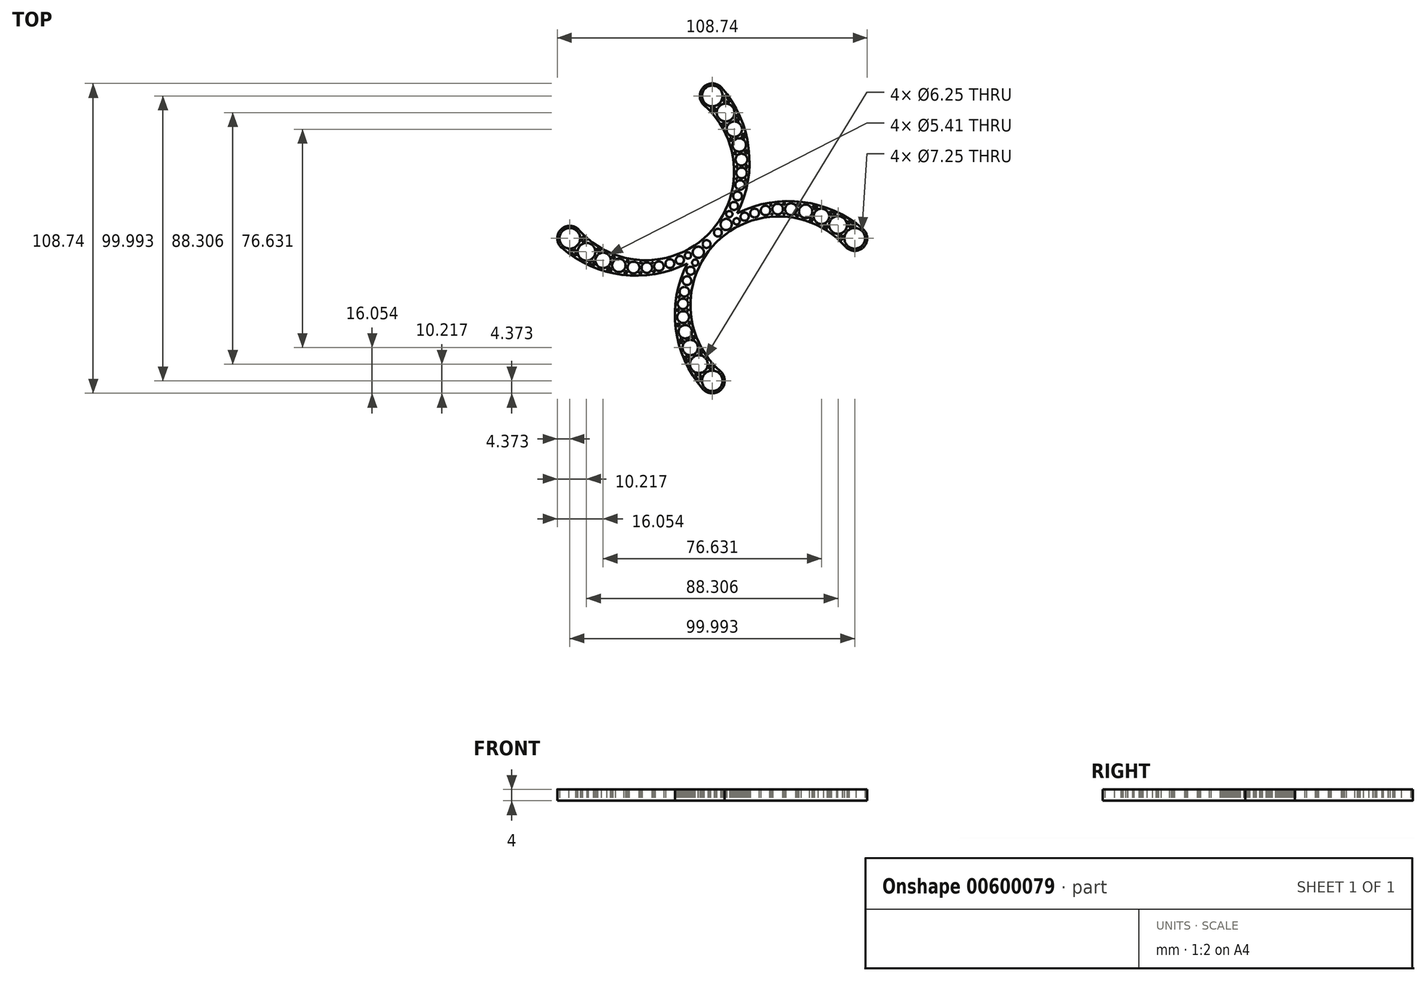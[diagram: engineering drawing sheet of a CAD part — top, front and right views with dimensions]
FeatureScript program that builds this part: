
annotation { "Feature Type Name" : "Feature", "Feature Type Description" : "" }
export const myFeature = defineFeature(function(context is Context, id is Id, definition is map)
    precondition{}
    {
        {
            var Q0;
            Q0=qCreatedBy(makeId("Top.planeOp"),FACE);
            var sketch = newSketch(context, id + "F0", { "sketchPlane" : qUnion([Q0])});
            skCircle(sketch, "E0.1.0", {"center": v(-50, 0) * mm, "radius": 3.62 * mm});
            skArc(sketch, "E0.1.1", {"start": v(-50.38, -4.36) * mm, "mid": v(-49.12, -4.29) * mm, "end": v(-47.93, -3.86) * mm});
            skArc(sketch, "E1", {"start": v(-46.7, 2.89) * mm, "mid": v(-24.38, -7.66) * mm, "end": v(-1.41, 1.41) * mm});
            skArc(sketch, "E2", {"start": v(-52.87, -3.3) * mm, "mid": v(-31.68, -12.77) * mm, "end": v(-8.81, -8.81) * mm});
            skArc(sketch, "E3.0", {"start": v(-50.38, -4.36) * mm, "mid": v(-49.07, -5.31) * mm, "end": v(-47.72, -6.21) * mm});
            skArc(sketch, "E4.0", {"start": v(-45.68, 0.7) * mm, "mid": v(-44.86, -0.08) * mm, "end": v(-44, -0.83) * mm});
            skPoint(sketch, "E5.orphan", {"position": v(-52.38, -2.74) * mm});
            skPoint(sketch, "E6.orphan", {"position": v(-47.27, 2.4) * mm});
            skArc(sketch, "E7.trimOffspring", {"start": v(-46.7, 2.89) * mm, "mid": v(-53.1, 3.09) * mm, "end": v(-52.87, -3.3) * mm});
            skArc(sketch, "E8", {"start": v(-47.93, -3.86) * mm, "mid": v(-48.01, -5.05) * mm, "end": v(-47.72, -6.21) * mm});
            skArc(sketch, "E9", {"start": v(-41.77, -7.75) * mm, "mid": v(-41.64, -8.67) * mm, "end": v(-41.27, -9.52) * mm});
            skCircle(sketch, "E10.0", {"center": v(-44.15, -4.7) * mm, "radius": 3.12 * mm});
            skCircle(sketch, "E11.0", {"center": v(-38.32, -7.73) * mm, "radius": 2.7 * mm});
            skArc(sketch, "E12", {"start": v(-33.98, -6.6) * mm, "mid": v(-34.47, -6.87) * mm, "end": v(-34.9, -7.2) * mm});
            skArc(sketch, "E13", {"start": v(-29.22, -7.89) * mm, "mid": v(-29.55, -8.15) * mm, "end": v(-29.84, -8.45) * mm});
            skArc(sketch, "E14", {"start": v(-24.77, -8.4) * mm, "mid": v(-24.98, -8.63) * mm, "end": v(-25.16, -8.89) * mm});
            skCircle(sketch, "E15.0", {"center": v(-32.77, -9.47) * mm, "radius": 2.36 * mm});
            skCircle(sketch, "E16.0", {"center": v(-27.65, -10.24) * mm, "radius": 2.08 * mm});
            skCircle(sketch, "E17.0", {"center": v(-22.97, -10.28) * mm, "radius": 1.85 * mm});
            skArc(sketch, "E18", {"start": v(-20.65, -8.31) * mm, "mid": v(-20.78, -8.5) * mm, "end": v(-20.9, -8.7) * mm});
            skCircle(sketch, "E19.0", {"center": v(-18.72, -9.78) * mm, "radius": 1.67 * mm});
            skCircle(sketch, "E20.0", {"center": v(-14.87, -8.86) * mm, "radius": 1.54 * mm});
            skCircle(sketch, "E21.0", {"center": v(-11.37, -7.62) * mm, "radius": 1.43 * mm});
            skCircle(sketch, "E22.0", {"center": v(-8.52, -5.99) * mm, "radius": 1.1 * mm});
            skCircle(sketch, "E23.0", {"center": v(-4.88, -4.88) * mm, "radius": 1.96 * mm});
            skCircle(sketch, "E24.0", {"center": v(-2, -2) * mm, "radius": 1.37 * mm});
            skArc(sketch, "E25.trimOffspring", {"start": v(-45.79, -1.19) * mm, "mid": v(-45.63, -0.25) * mm, "end": v(-45.68, 0.7) * mm});
            skArc(sketch, "E26.trimOffspring", {"start": v(-44, -0.83) * mm, "mid": v(-44.92, -0.9) * mm, "end": v(-45.79, -1.19) * mm});
            skArc(sketch, "E27.trimOffspring", {"start": v(-40.5, -3.43) * mm, "mid": v(-39.74, -3.9) * mm, "end": v(-38.97, -4.34) * mm});
            skArc(sketch, "E28.trimOffspring", {"start": v(-43.54, -8.53) * mm, "mid": v(-42.41, -9.04) * mm, "end": v(-41.27, -9.52) * mm});
            skArc(sketch, "E29.trimOffspring", {"start": v(-43.54, -8.53) * mm, "mid": v(-42.6, -8.25) * mm, "end": v(-41.77, -7.75) * mm});
            skArc(sketch, "E30.trimOffspring", {"start": v(-35.26, -6.13) * mm, "mid": v(-34.62, -6.37) * mm, "end": v(-33.98, -6.6) * mm});
            skArc(sketch, "E31.trimOffspring", {"start": v(-38.97, -4.34) * mm, "mid": v(-39.66, -4.55) * mm, "end": v(-40.28, -4.9) * mm});
            skArc(sketch, "E32.trimOffspring", {"start": v(-40.28, -4.9) * mm, "mid": v(-40.32, -4.15) * mm, "end": v(-40.5, -3.43) * mm});
            skArc(sketch, "E33.trimOffspring", {"start": v(-37.05, -10.94) * mm, "mid": v(-36.38, -10.6) * mm, "end": v(-35.81, -10.1) * mm});
            skArc(sketch, "E34.trimOffspring", {"start": v(-37.05, -10.94) * mm, "mid": v(-36.13, -11.18) * mm, "end": v(-35.2, -11.4) * mm});
            skArc(sketch, "E35.trimOffspring", {"start": v(-30.23, -7.68) * mm, "mid": v(-29.73, -7.79) * mm, "end": v(-29.22, -7.89) * mm});
            skArc(sketch, "E36.trimOffspring", {"start": v(-34.9, -7.2) * mm, "mid": v(-35.04, -6.65) * mm, "end": v(-35.26, -6.13) * mm});
            skArc(sketch, "E37.trimOffspring", {"start": v(-35.81, -10.1) * mm, "mid": v(-35.59, -10.79) * mm, "end": v(-35.2, -11.4) * mm});
            skArc(sketch, "E38.trimOffspring", {"start": v(-31.1, -12.08) * mm, "mid": v(-30.38, -12.16) * mm, "end": v(-29.66, -12.22) * mm});
            skArc(sketch, "E39.trimOffspring", {"start": v(-31.1, -12.08) * mm, "mid": v(-30.64, -11.73) * mm, "end": v(-30.26, -11.3) * mm});
            skArc(sketch, "E40.trimOffspring", {"start": v(-30.26, -11.3) * mm, "mid": v(-30, -11.79) * mm, "end": v(-29.66, -12.22) * mm});
            skArc(sketch, "E41.trimOffspring", {"start": v(-29.84, -8.45) * mm, "mid": v(-30, -8.05) * mm, "end": v(-30.23, -7.68) * mm});
            skArc(sketch, "E42.trimOffspring", {"start": v(-25.19, -11.64) * mm, "mid": v(-24.94, -11.97) * mm, "end": v(-24.65, -12.27) * mm});
            skArc(sketch, "E43.trimOffspring", {"start": v(-25.16, -8.89) * mm, "mid": v(-25.33, -8.61) * mm, "end": v(-25.53, -8.36) * mm});
            skArc(sketch, "E44.trimOffspring", {"start": v(-20.58, -11.33) * mm, "mid": v(-20.37, -11.56) * mm, "end": v(-20.12, -11.76) * mm});
            skArc(sketch, "E45.trimOffspring", {"start": v(-20.9, -8.7) * mm, "mid": v(-21.04, -8.53) * mm, "end": v(-21.21, -8.36) * mm});
            skArc(sketch, "E46.trimOffspring", {"start": v(-21.21, -8.36) * mm, "mid": v(-20.93, -8.34) * mm, "end": v(-20.65, -8.31) * mm});
            skArc(sketch, "E47.trimOffspring", {"start": v(-25.73, -12.31) * mm, "mid": v(-25.19, -12.3) * mm, "end": v(-24.65, -12.27) * mm});
            skArc(sketch, "E48.trimOffspring", {"start": v(-25.73, -12.31) * mm, "mid": v(-25.43, -12) * mm, "end": v(-25.19, -11.64) * mm});
            skArc(sketch, "E49.trimOffspring", {"start": v(-20.92, -11.89) * mm, "mid": v(-20.73, -11.62) * mm, "end": v(-20.58, -11.33) * mm});
            skArc(sketch, "E50.trimOffspring", {"start": v(-20.92, -11.89) * mm, "mid": v(-20.52, -11.83) * mm, "end": v(-20.12, -11.76) * mm});
            skLineSegment(sketch, "E51", {"start": v(-25.53, -8.36) * mm, "end": v(-24.77, -8.4) * mm});
            skArc(sketch, "E52.2.MirrorCS", {"start": v(-6.6, -33.98) * mm, "mid": v(-6.87, -34.47) * mm, "end": v(-7.2, -34.9) * mm});
            skArc(sketch, "E52.3.MirrorCS", {"start": v(-7.2, -34.9) * mm, "mid": v(-6.65, -35.04) * mm, "end": v(-6.13, -35.26) * mm});
            skCircle(sketch, "E52.4.MirrorC", {"center": v(-5.99, -8.52) * mm, "radius": 1.1 * mm});
            skArc(sketch, "E52.8.MirrorCS", {"start": v(-6.13, -35.26) * mm, "mid": v(-6.37, -34.62) * mm, "end": v(-6.6, -33.98) * mm});
            skArc(sketch, "E52.9.MirrorCS", {"start": v(-11.89, -20.92) * mm, "mid": v(-11.62, -20.73) * mm, "end": v(-11.33, -20.58) * mm});
            skArc(sketch, "E52.10.MirrorCS", {"start": v(-8.89, -25.16) * mm, "mid": v(-8.61, -25.33) * mm, "end": v(-8.36, -25.53) * mm});
            skArc(sketch, "E52.11.MirrorCS", {"start": v(-8.4, -24.77) * mm, "mid": v(-8.63, -24.98) * mm, "end": v(-8.89, -25.16) * mm});
            skLineSegment(sketch, "E52.13.MirrorCS", {"start": v(-8.36, -25.53) * mm, "end": v(-8.4, -24.77) * mm});
            skArc(sketch, "E52.14.MirrorCS", {"start": v(-8.31, -20.65) * mm, "mid": v(-8.5, -20.78) * mm, "end": v(-8.7, -20.9) * mm});
            skArc(sketch, "E52.18.MirrorCS", {"start": v(-10.1, -35.81) * mm, "mid": v(-10.79, -35.59) * mm, "end": v(-11.4, -35.2) * mm});
            skArc(sketch, "E52.19.MirrorCS", {"start": v(-10.94, -37.05) * mm, "mid": v(-10.6, -36.38) * mm, "end": v(-10.1, -35.81) * mm});
            skCircle(sketch, "E52.20.MirrorC", {"center": v(-7.62, -11.37) * mm, "radius": 1.43 * mm});
            skArc(sketch, "E52.21.MirrorCS", {"start": v(-10.94, -37.05) * mm, "mid": v(-11.18, -36.13) * mm, "end": v(-11.4, -35.2) * mm});
            skArc(sketch, "E52.22.MirrorCS", {"start": v(-4.36, -50.38) * mm, "mid": v(-5.31, -49.07) * mm, "end": v(-6.21, -47.72) * mm});
            skArc(sketch, "E52.23.MirrorCS", {"start": v(0.7, -45.68) * mm, "mid": v(-0.08, -44.86) * mm, "end": v(-0.83, -44) * mm});
            skArc(sketch, "E52.24.MirrorCS", {"start": v(-4.36, -50.38) * mm, "mid": v(-4.29, -49.12) * mm, "end": v(-3.86, -47.93) * mm});
            skArc(sketch, "E52.25.MirrorCS", {"start": v(-11.89, -20.92) * mm, "mid": v(-11.83, -20.52) * mm, "end": v(-11.76, -20.12) * mm});
            skArc(sketch, "E52.27.MirrorCS", {"start": v(-12.31, -25.73) * mm, "mid": v(-12, -25.43) * mm, "end": v(-11.64, -25.19) * mm});
            skArc(sketch, "E52.28.MirrorCS", {"start": v(-12.08, -31.1) * mm, "mid": v(-11.73, -30.64) * mm, "end": v(-11.3, -30.26) * mm});
            skCircle(sketch, "E52.29.MirrorC", {"center": v(-8.86, -14.87) * mm, "radius": 1.54 * mm});
            skArc(sketch, "E52.30.MirrorCS", {"start": v(-12.08, -31.1) * mm, "mid": v(-12.16, -30.38) * mm, "end": v(-12.22, -29.66) * mm});
            skArc(sketch, "E52.31.MirrorCS", {"start": v(-7.68, -30.23) * mm, "mid": v(-7.79, -29.73) * mm, "end": v(-7.89, -29.22) * mm});
            skArc(sketch, "E52.32.MirrorCS", {"start": v(-11.33, -20.58) * mm, "mid": v(-11.56, -20.37) * mm, "end": v(-11.76, -20.12) * mm});
            skArc(sketch, "E52.34.MirrorCS", {"start": v(-12.31, -25.73) * mm, "mid": v(-12.3, -25.19) * mm, "end": v(-12.27, -24.65) * mm});
            skArc(sketch, "E52.35.MirrorCS", {"start": v(-8.36, -21.21) * mm, "mid": v(-8.34, -20.93) * mm, "end": v(-8.31, -20.65) * mm});
            skArc(sketch, "E52.37.MirrorCS", {"start": v(-11.3, -30.26) * mm, "mid": v(-11.79, -30) * mm, "end": v(-12.22, -29.66) * mm});
            skArc(sketch, "E52.38.MirrorCS", {"start": v(-3.86, -47.93) * mm, "mid": v(-5.05, -48.01) * mm, "end": v(-6.21, -47.72) * mm});
            skArc(sketch, "E52.41.MirrorCS", {"start": v(-1.19, -45.79) * mm, "mid": v(-0.25, -45.63) * mm, "end": v(0.7, -45.68) * mm});
            skArc(sketch, "E52.42.MirrorCS", {"start": v(-8.45, -29.84) * mm, "mid": v(-8.05, -30) * mm, "end": v(-7.68, -30.23) * mm});
            skArc(sketch, "E52.43.MirrorCS", {"start": v(-7.89, -29.22) * mm, "mid": v(-8.15, -29.55) * mm, "end": v(-8.45, -29.84) * mm});
            skArc(sketch, "E52.44.MirrorCS", {"start": v(-11.64, -25.19) * mm, "mid": v(-11.97, -24.94) * mm, "end": v(-12.27, -24.65) * mm});
            skArc(sketch, "E52.47.MirrorCS", {"start": v(-8.7, -20.9) * mm, "mid": v(-8.53, -21.04) * mm, "end": v(-8.36, -21.21) * mm});
            skArc(sketch, "E52.48.MirrorCS", {"start": v(-4.9, -40.28) * mm, "mid": v(-4.15, -40.32) * mm, "end": v(-3.43, -40.5) * mm});
            skArc(sketch, "E52.49.MirrorCS", {"start": v(-7.75, -41.77) * mm, "mid": v(-8.67, -41.64) * mm, "end": v(-9.52, -41.27) * mm});
            skArc(sketch, "E52.50.MirrorCS", {"start": v(-8.53, -43.54) * mm, "mid": v(-9.04, -42.41) * mm, "end": v(-9.52, -41.27) * mm});
            skArc(sketch, "E52.51.MirrorCS", {"start": v(-4.34, -38.97) * mm, "mid": v(-4.55, -39.66) * mm, "end": v(-4.9, -40.28) * mm});
            skArc(sketch, "E52.52.MirrorCS", {"start": v(-3.43, -40.5) * mm, "mid": v(-3.9, -39.74) * mm, "end": v(-4.34, -38.97) * mm});
            skArc(sketch, "E52.53.MirrorCS", {"start": v(-0.83, -44) * mm, "mid": v(-0.9, -44.92) * mm, "end": v(-1.19, -45.79) * mm});
            skArc(sketch, "E52.54.MirrorCS", {"start": v(-8.53, -43.54) * mm, "mid": v(-8.25, -42.6) * mm, "end": v(-7.75, -41.77) * mm});
            skPoint(sketch, "E52.55.MirrorP", {"position": v(2.4, -47.27) * mm});
            skArc(sketch, "E52.56.MirrorCS", {"start": v(-3.3, -52.87) * mm, "mid": v(-12.77, -31.68) * mm, "end": v(-8.81, -8.81) * mm});
            skCircle(sketch, "E52.57.MirrorC", {"center": v(0, -50) * mm, "radius": 3.62 * mm});
            skCircle(sketch, "E52.58.MirrorC", {"center": v(-7.73, -38.32) * mm, "radius": 2.7 * mm});
            skCircle(sketch, "E52.59.MirrorC", {"center": v(-10.28, -22.97) * mm, "radius": 1.85 * mm});
            skArc(sketch, "E52.60.MirrorCS", {"start": v(2.89, -46.7) * mm, "mid": v(3.09, -53.1) * mm, "end": v(-3.3, -52.87) * mm});
            skCircle(sketch, "E52.61.MirrorC", {"center": v(-9.78, -18.72) * mm, "radius": 1.67 * mm});
            skCircle(sketch, "E52.62.MirrorC", {"center": v(-4.7, -44.15) * mm, "radius": 3.12 * mm});
            skCircle(sketch, "E52.63.MirrorC", {"center": v(-9.47, -32.77) * mm, "radius": 2.36 * mm});
            skCircle(sketch, "E52.64.MirrorC", {"center": v(-10.24, -27.65) * mm, "radius": 2.08 * mm});
            skPoint(sketch, "E52.65.MirrorP", {"position": v(-2.74, -52.38) * mm});
            skArc(sketch, "E53.0.MirrorCS", {"start": v(2.89, -46.7) * mm, "mid": v(-7.66, -24.38) * mm, "end": v(1.41, -1.41) * mm});
            skLineSegment(sketch, "E54.11.MirrorCS", {"start": v(8.36, 25.53) * mm, "end": v(8.4, 24.77) * mm});
            skCircle(sketch, "E54.13.MirrorC", {"center": v(5.99, 8.52) * mm, "radius": 1.1 * mm});
            skCircle(sketch, "E54.15.MirrorC", {"center": v(7.62, 11.37) * mm, "radius": 1.43 * mm});
            skArc(sketch, "E54.20.MirrorCS", {"start": v(8.36, 21.21) * mm, "mid": v(8.34, 20.93) * mm, "end": v(8.31, 20.65) * mm});
            skArc(sketch, "E54.21.MirrorCS", {"start": v(20.65, 8.31) * mm, "mid": v(20.78, 8.5) * mm, "end": v(20.9, 8.7) * mm});
            skArc(sketch, "E54.22.MirrorCS", {"start": v(25.19, 11.64) * mm, "mid": v(24.94, 11.97) * mm, "end": v(24.65, 12.27) * mm});
            skArc(sketch, "E54.23.MirrorCS", {"start": v(8.4, 24.77) * mm, "mid": v(8.63, 24.98) * mm, "end": v(8.89, 25.16) * mm});
            skArc(sketch, "E54.25.MirrorCS", {"start": v(11.33, 20.58) * mm, "mid": v(11.56, 20.37) * mm, "end": v(11.76, 20.12) * mm});
            skArc(sketch, "E54.27.MirrorCS", {"start": v(12.31, 25.73) * mm, "mid": v(12, 25.43) * mm, "end": v(11.64, 25.19) * mm});
            skArc(sketch, "E54.31.MirrorCS", {"start": v(8.89, 25.16) * mm, "mid": v(8.61, 25.33) * mm, "end": v(8.36, 25.53) * mm});
            skArc(sketch, "E54.33.MirrorCS", {"start": v(8.7, 20.9) * mm, "mid": v(8.53, 21.04) * mm, "end": v(8.36, 21.21) * mm});
            skArc(sketch, "E54.34.MirrorCS", {"start": v(12.31, 25.73) * mm, "mid": v(12.3, 25.19) * mm, "end": v(12.27, 24.65) * mm});
            skArc(sketch, "E54.35.MirrorCS", {"start": v(20.9, 8.7) * mm, "mid": v(21.04, 8.53) * mm, "end": v(21.21, 8.36) * mm});
            skArc(sketch, "E54.36.MirrorCS", {"start": v(30.23, 7.68) * mm, "mid": v(29.73, 7.79) * mm, "end": v(29.22, 7.89) * mm});
            skArc(sketch, "E54.37.MirrorCS", {"start": v(7.68, 30.23) * mm, "mid": v(7.79, 29.73) * mm, "end": v(7.89, 29.22) * mm});
            skArc(sketch, "E54.38.MirrorCS", {"start": v(8.31, 20.65) * mm, "mid": v(8.5, 20.78) * mm, "end": v(8.7, 20.9) * mm});
            skArc(sketch, "E54.41.MirrorCS", {"start": v(11.64, 25.19) * mm, "mid": v(11.97, 24.94) * mm, "end": v(12.27, 24.65) * mm});
            skCircle(sketch, "E54.42.MirrorC", {"center": v(14.87, 8.86) * mm, "radius": 1.54 * mm});
            skCircle(sketch, "E54.44.MirrorC", {"center": v(8.52, 5.99) * mm, "radius": 1.1 * mm});
            skArc(sketch, "E54.47.MirrorCS", {"start": v(10.1, 35.81) * mm, "mid": v(10.79, 35.59) * mm, "end": v(11.4, 35.2) * mm});
            skArc(sketch, "E54.48.MirrorCS", {"start": v(4.36, 50.38) * mm, "mid": v(4.29, 49.12) * mm, "end": v(3.86, 47.93) * mm});
            skArc(sketch, "E54.49.MirrorCS", {"start": v(10.94, 37.05) * mm, "mid": v(11.18, 36.13) * mm, "end": v(11.4, 35.2) * mm});
            skArc(sketch, "E54.50.MirrorCS", {"start": v(29.84, 8.45) * mm, "mid": v(30, 8.05) * mm, "end": v(30.23, 7.68) * mm});
            skArc(sketch, "E54.51.MirrorCS", {"start": v(31.1, 12.08) * mm, "mid": v(30.38, 12.16) * mm, "end": v(29.66, 12.22) * mm});
            skCircle(sketch, "E54.53.MirrorC", {"center": v(18.72, 9.78) * mm, "radius": 1.67 * mm});
            skArc(sketch, "E54.54.MirrorCS", {"start": v(-0.7, 45.68) * mm, "mid": v(0.08, 44.86) * mm, "end": v(0.83, 44) * mm});
            skArc(sketch, "E54.55.MirrorCS", {"start": v(4.36, 50.38) * mm, "mid": v(5.31, 49.07) * mm, "end": v(6.21, 47.72) * mm});
            skArc(sketch, "E54.56.MirrorCS", {"start": v(3.86, 47.93) * mm, "mid": v(5.05, 48.01) * mm, "end": v(6.21, 47.72) * mm});
            skArc(sketch, "E54.57.MirrorCS", {"start": v(7.89, 29.22) * mm, "mid": v(8.15, 29.55) * mm, "end": v(8.45, 29.84) * mm});
            skArc(sketch, "E54.59.MirrorCS", {"start": v(6.13, 35.26) * mm, "mid": v(6.37, 34.62) * mm, "end": v(6.6, 33.98) * mm});
            skArc(sketch, "E54.62.MirrorCS", {"start": v(11.89, 20.92) * mm, "mid": v(11.62, 20.73) * mm, "end": v(11.33, 20.58) * mm});
            skArc(sketch, "E54.63.MirrorCS", {"start": v(35.26, 6.13) * mm, "mid": v(34.62, 6.37) * mm, "end": v(33.98, 6.6) * mm});
            skArc(sketch, "E54.64.MirrorCS", {"start": v(25.73, 12.31) * mm, "mid": v(25.43, 12) * mm, "end": v(25.19, 11.64) * mm});
            skArc(sketch, "E54.65.MirrorCS", {"start": v(10.94, 37.05) * mm, "mid": v(10.6, 36.38) * mm, "end": v(10.1, 35.81) * mm});
            skArc(sketch, "E54.66.MirrorCS", {"start": v(29.22, 7.89) * mm, "mid": v(29.55, 8.15) * mm, "end": v(29.84, 8.45) * mm});
            skArc(sketch, "E54.67.MirrorCS", {"start": v(6.6, 33.98) * mm, "mid": v(6.87, 34.47) * mm, "end": v(7.2, 34.9) * mm});
            skCircle(sketch, "E54.68.MirrorC", {"center": v(4.88, 4.88) * mm, "radius": 1.96 * mm});
            skArc(sketch, "E54.69.MirrorCS", {"start": v(7.2, 34.9) * mm, "mid": v(6.65, 35.04) * mm, "end": v(6.13, 35.26) * mm});
            skArc(sketch, "E54.70.MirrorCS", {"start": v(20.58, 11.33) * mm, "mid": v(20.37, 11.56) * mm, "end": v(20.12, 11.76) * mm});
            skArc(sketch, "E54.71.MirrorCS", {"start": v(34.9, 7.2) * mm, "mid": v(35.04, 6.65) * mm, "end": v(35.26, 6.13) * mm});
            skArc(sketch, "E54.72.MirrorCS", {"start": v(40.28, 4.9) * mm, "mid": v(40.32, 4.15) * mm, "end": v(40.5, 3.43) * mm});
            skArc(sketch, "E54.73.MirrorCS", {"start": v(4.9, 40.28) * mm, "mid": v(4.15, 40.32) * mm, "end": v(3.43, 40.5) * mm});
            skCircle(sketch, "E54.74.MirrorC", {"center": v(8.86, 14.87) * mm, "radius": 1.54 * mm});
            skArc(sketch, "E54.76.MirrorCS", {"start": v(38.97, 4.34) * mm, "mid": v(39.66, 4.55) * mm, "end": v(40.28, 4.9) * mm});
            skArc(sketch, "E54.77.MirrorCS", {"start": v(21.21, 8.36) * mm, "mid": v(20.93, 8.34) * mm, "end": v(20.65, 8.31) * mm});
            skArc(sketch, "E54.78.MirrorCS", {"start": v(1.19, 45.79) * mm, "mid": v(0.25, 45.63) * mm, "end": v(-0.7, 45.68) * mm});
            skArc(sketch, "E54.80.MirrorCS", {"start": v(25.73, 12.31) * mm, "mid": v(25.19, 12.3) * mm, "end": v(24.65, 12.27) * mm});
            skArc(sketch, "E54.81.MirrorCS", {"start": v(33.98, 6.6) * mm, "mid": v(34.47, 6.87) * mm, "end": v(34.9, 7.2) * mm});
            skArc(sketch, "E54.82.MirrorCS", {"start": v(45.68, -0.7) * mm, "mid": v(44.86, 0.08) * mm, "end": v(44, 0.83) * mm});
            skArc(sketch, "E54.83.MirrorCS", {"start": v(20.92, 11.89) * mm, "mid": v(20.73, 11.62) * mm, "end": v(20.58, 11.33) * mm});
            skArc(sketch, "E54.84.MirrorCS", {"start": v(20.92, 11.89) * mm, "mid": v(20.52, 11.83) * mm, "end": v(20.12, 11.76) * mm});
            skArc(sketch, "E54.85.MirrorCS", {"start": v(45.79, 1.19) * mm, "mid": v(45.63, 0.25) * mm, "end": v(45.68, -0.7) * mm});
            skArc(sketch, "E54.86.MirrorCS", {"start": v(12.08, 31.1) * mm, "mid": v(11.73, 30.64) * mm, "end": v(11.3, 30.26) * mm});
            skCircle(sketch, "E54.89.MirrorC", {"center": v(11.37, 7.62) * mm, "radius": 1.43 * mm});
            skArc(sketch, "E54.90.MirrorCS", {"start": v(4.34, 38.97) * mm, "mid": v(4.55, 39.66) * mm, "end": v(4.9, 40.28) * mm});
            skCircle(sketch, "E54.91.MirrorC", {"center": v(9.78, 18.72) * mm, "radius": 1.67 * mm});
            skArc(sketch, "E54.92.MirrorCS", {"start": v(25.16, 8.89) * mm, "mid": v(25.33, 8.61) * mm, "end": v(25.53, 8.36) * mm});
            skArc(sketch, "E54.93.MirrorCS", {"start": v(11.89, 20.92) * mm, "mid": v(11.83, 20.52) * mm, "end": v(11.76, 20.12) * mm});
            skArc(sketch, "E54.94.MirrorCS", {"start": v(8.45, 29.84) * mm, "mid": v(8.05, 30) * mm, "end": v(7.68, 30.23) * mm});
            skArc(sketch, "E54.95.MirrorCS", {"start": v(3.43, 40.5) * mm, "mid": v(3.9, 39.74) * mm, "end": v(4.34, 38.97) * mm});
            skCircle(sketch, "E54.96.MirrorC", {"center": v(7.73, 38.32) * mm, "radius": 2.7 * mm});
            skArc(sketch, "E54.97.MirrorCS", {"start": v(44, 0.83) * mm, "mid": v(44.92, 0.9) * mm, "end": v(45.79, 1.19) * mm});
            skArc(sketch, "E54.98.MirrorCS", {"start": v(37.05, 10.94) * mm, "mid": v(36.13, 11.18) * mm, "end": v(35.2, 11.4) * mm});
            skArc(sketch, "E54.99.MirrorCS", {"start": v(30.26, 11.3) * mm, "mid": v(30, 11.79) * mm, "end": v(29.66, 12.22) * mm});
            skArc(sketch, "E54.100.MirrorCS", {"start": v(12.08, 31.1) * mm, "mid": v(12.16, 30.38) * mm, "end": v(12.22, 29.66) * mm});
            skArc(sketch, "E54.101.MirrorCS", {"start": v(43.54, 8.53) * mm, "mid": v(42.6, 8.25) * mm, "end": v(41.77, 7.75) * mm});
            skCircle(sketch, "E54.102.MirrorC", {"center": v(4.7, 44.15) * mm, "radius": 3.12 * mm});
            skCircle(sketch, "E54.103.MirrorC", {"center": v(9.47, 32.77) * mm, "radius": 2.36 * mm});
            skArc(sketch, "E54.104.MirrorCS", {"start": v(40.5, 3.43) * mm, "mid": v(39.74, 3.9) * mm, "end": v(38.97, 4.34) * mm});
            skArc(sketch, "E54.105.MirrorCS", {"start": v(41.77, 7.75) * mm, "mid": v(41.64, 8.67) * mm, "end": v(41.27, 9.52) * mm});
            skArc(sketch, "E54.106.MirrorCS", {"start": v(50.38, 4.36) * mm, "mid": v(49.12, 4.29) * mm, "end": v(47.93, 3.86) * mm});
            skArc(sketch, "E54.107.MirrorCS", {"start": v(7.75, 41.77) * mm, "mid": v(8.67, 41.64) * mm, "end": v(9.52, 41.27) * mm});
            skArc(sketch, "E54.108.MirrorCS", {"start": v(47.93, 3.86) * mm, "mid": v(48.01, 5.05) * mm, "end": v(47.72, 6.21) * mm});
            skCircle(sketch, "E54.109.MirrorC", {"center": v(22.97, 10.28) * mm, "radius": 1.85 * mm});
            skCircle(sketch, "E54.110.MirrorC", {"center": v(2, 2) * mm, "radius": 1.37 * mm});
            skLineSegment(sketch, "E54.111.MirrorCS", {"start": v(25.53, 8.36) * mm, "end": v(24.77, 8.4) * mm});
            skArc(sketch, "E54.112.MirrorCS", {"start": v(37.05, 10.94) * mm, "mid": v(36.38, 10.6) * mm, "end": v(35.81, 10.1) * mm});
            skArc(sketch, "E54.113.MirrorCS", {"start": v(8.53, 43.54) * mm, "mid": v(8.25, 42.6) * mm, "end": v(7.75, 41.77) * mm});
            skArc(sketch, "E54.114.MirrorCS", {"start": v(35.81, 10.1) * mm, "mid": v(35.59, 10.79) * mm, "end": v(35.2, 11.4) * mm});
            skArc(sketch, "E54.115.MirrorCS", {"start": v(43.54, 8.53) * mm, "mid": v(42.41, 9.04) * mm, "end": v(41.27, 9.52) * mm});
            skArc(sketch, "E54.116.MirrorCS", {"start": v(50.38, 4.36) * mm, "mid": v(49.07, 5.31) * mm, "end": v(47.72, 6.21) * mm});
            skArc(sketch, "E54.117.MirrorCS", {"start": v(31.1, 12.08) * mm, "mid": v(30.64, 11.73) * mm, "end": v(30.26, 11.3) * mm});
            skCircle(sketch, "E54.118.MirrorC", {"center": v(10.24, 27.65) * mm, "radius": 2.08 * mm});
            skArc(sketch, "E54.119.MirrorCS", {"start": v(0.83, 44) * mm, "mid": v(0.9, 44.92) * mm, "end": v(1.19, 45.79) * mm});
            skArc(sketch, "E54.120.MirrorCS", {"start": v(8.53, 43.54) * mm, "mid": v(9.04, 42.41) * mm, "end": v(9.52, 41.27) * mm});
            skCircle(sketch, "E54.121.MirrorC", {"center": v(10.28, 22.97) * mm, "radius": 1.85 * mm});
            skArc(sketch, "E54.122.MirrorCS", {"start": v(24.77, 8.4) * mm, "mid": v(24.98, 8.63) * mm, "end": v(25.16, 8.89) * mm});
            skCircle(sketch, "E54.123.MirrorC", {"center": v(0, 50) * mm, "radius": 3.62 * mm});
            skArc(sketch, "E54.124.MirrorCS", {"start": v(3.3, 52.87) * mm, "mid": v(12.77, 31.68) * mm, "end": v(8.81, 8.81) * mm});
            skArc(sketch, "E54.125.MirrorCS", {"start": v(-2.89, 46.7) * mm, "mid": v(7.66, 24.38) * mm, "end": v(-1.41, 1.41) * mm});
            skArc(sketch, "E54.126.MirrorCS", {"start": v(-2.89, 46.7) * mm, "mid": v(-3.09, 53.1) * mm, "end": v(3.3, 52.87) * mm});
            skCircle(sketch, "E54.127.MirrorC", {"center": v(50, 0) * mm, "radius": 3.62 * mm});
            skPoint(sketch, "E54.128.MirrorP", {"position": v(2.74, 52.38) * mm});
            skPoint(sketch, "E54.129.MirrorP", {"position": v(47.27, -2.4) * mm});
            skArc(sketch, "E54.130.MirrorCS", {"start": v(46.7, -2.89) * mm, "mid": v(24.38, 7.66) * mm, "end": v(1.41, -1.41) * mm});
            skPoint(sketch, "E54.131.MirrorP", {"position": v(-2.4, 47.27) * mm});
            skArc(sketch, "E54.132.MirrorCS", {"start": v(52.87, 3.3) * mm, "mid": v(31.68, 12.77) * mm, "end": v(8.81, 8.81) * mm});
            skCircle(sketch, "E54.133.MirrorC", {"center": v(27.65, 10.24) * mm, "radius": 2.08 * mm});
            skCircle(sketch, "E54.134.MirrorC", {"center": v(38.32, 7.73) * mm, "radius": 2.7 * mm});
            skPoint(sketch, "E54.135.MirrorP", {"position": v(52.38, 2.74) * mm});
            skCircle(sketch, "E54.136.MirrorC", {"center": v(44.15, 4.7) * mm, "radius": 3.12 * mm});
            skCircle(sketch, "E54.137.MirrorC", {"center": v(32.77, 9.47) * mm, "radius": 2.36 * mm});
            skArc(sketch, "E54.138.MirrorCS", {"start": v(46.7, -2.89) * mm, "mid": v(53.1, -3.09) * mm, "end": v(52.87, 3.3) * mm});
            skArc(sketch, "E54.139.MirrorCS", {"start": v(11.3, 30.26) * mm, "mid": v(11.79, 30) * mm, "end": v(12.22, 29.66) * mm});
            skSolve(sketch);
        }
        {
            var Q0;
            Q0=qSketchRegion(id+"F0",true);
            extrude(context, id + "F1", {"entities" : qUnion([Q0]), "depth" : 4 * mm});
        }
    });
